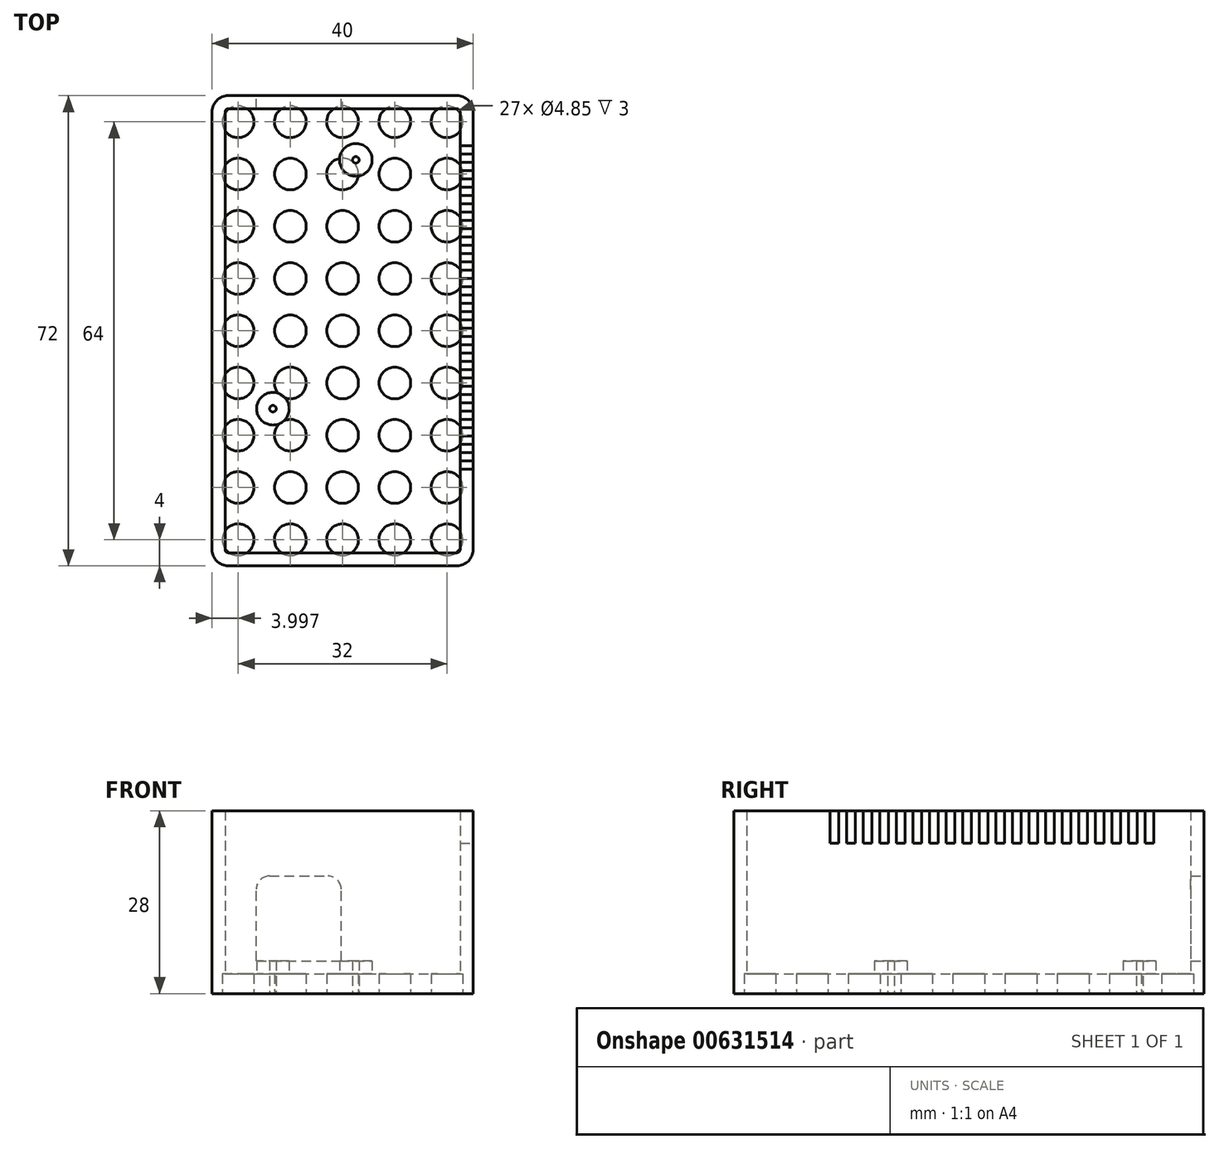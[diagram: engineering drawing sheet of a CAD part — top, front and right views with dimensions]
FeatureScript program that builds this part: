
annotation { "Feature Type Name" : "Feature", "Feature Type Description" : "" }
export const myFeature = defineFeature(function(context is Context, id is Id, definition is map)
    precondition{}
    {
        {
            var Q0;
            Q0=qCreatedBy(makeId("Top.planeOp"),FACE);
            var sketch = newSketch(context, id + "F0", { "sketchPlane" : qUnion([Q0])});
            skLineSegment(sketch, "E0", {"start": v(-12.71, -27.8) * mm, "end": v(-12.71, 30.62) * mm});
            skLineSegment(sketch, "E1", {"start": v(-12.71, 30.62) * mm, "end": v(15.23, 30.62) * mm});
            skLineSegment(sketch, "E2", {"start": v(15.23, -27.8) * mm, "end": v(15.23, 30.62) * mm});
            skLineSegment(sketch, "E3", {"start": v(-12.71, -27.8) * mm, "end": v(15.23, -27.8) * mm});
            skLineSegment(sketch, "E4", {"start": v(1, -18.66) * mm, "end": v(2.02, -18.66) * mm});
            skLineSegment(sketch, "E5", {"start": v(1.51, -19.16) * mm, "end": v(1.51, -18.15) * mm});
            skLineSegment(sketch, "E6", {"start": v(1, -16.12) * mm, "end": v(2.02, -16.12) * mm});
            skLineSegment(sketch, "E7", {"start": v(1.51, -16.62) * mm, "end": v(1.51, -15.6) * mm});
            skLineSegment(sketch, "E8", {"start": v(8.12, -3.92) * mm, "end": v(9.13, -3.92) * mm});
            skLineSegment(sketch, "E9", {"start": v(8.62, -4.43) * mm, "end": v(8.62, -3.42) * mm});
            skLineSegment(sketch, "E10", {"start": v(-11.7, -6.72) * mm, "end": v(-10.68, -6.72) * mm});
            skLineSegment(sketch, "E11", {"start": v(-11.19, -7.23) * mm, "end": v(-11.19, -6.21) * mm});
            skLineSegment(sketch, "E12", {"start": v(-9.16, -6.72) * mm, "end": v(-8.14, -6.72) * mm});
            skLineSegment(sketch, "E13", {"start": v(-8.65, -7.23) * mm, "end": v(-8.65, -6.21) * mm});
            skLineSegment(sketch, "E14", {"start": v(1.26, 12.46) * mm, "end": v(2.27, 12.46) * mm});
            skLineSegment(sketch, "E15", {"start": v(1.77, 11.95) * mm, "end": v(1.77, 12.97) * mm});
            skLineSegment(sketch, "E16", {"start": v(-1.28, 12.46) * mm, "end": v(-0.27, 12.46) * mm});
            skLineSegment(sketch, "E17", {"start": v(-0.77, 11.95) * mm, "end": v(-0.77, 12.97) * mm});
            skLineSegment(sketch, "E18", {"start": v(-4.87, 25.58) * mm, "end": v(-3.86, 25.58) * mm});
            skLineSegment(sketch, "E19", {"start": v(-4.37, 25.07) * mm, "end": v(-4.37, 26.09) * mm});
            skLineSegment(sketch, "E20", {"start": v(-9.27, 25.58) * mm, "end": v(-8.26, 25.58) * mm});
            skLineSegment(sketch, "E21", {"start": v(-8.77, 25.07) * mm, "end": v(-8.77, 26.09) * mm});
            skLineSegment(sketch, "E22", {"start": v(13.2, 16.4) * mm, "end": v(14.21, 16.4) * mm});
            skLineSegment(sketch, "E23", {"start": v(13.7, 15.89) * mm, "end": v(13.7, 16.9) * mm});
            skLineSegment(sketch, "E24", {"start": v(13.2, 18.94) * mm, "end": v(14.21, 18.94) * mm});
            skLineSegment(sketch, "E25", {"start": v(13.7, 18.43) * mm, "end": v(13.7, 19.44) * mm});
            skLineSegment(sketch, "E26", {"start": v(13.2, 21.48) * mm, "end": v(14.21, 21.48) * mm});
            skLineSegment(sketch, "E27", {"start": v(13.7, 20.97) * mm, "end": v(13.7, 21.98) * mm});
            skLineSegment(sketch, "E28", {"start": v(13.2, 24.02) * mm, "end": v(14.21, 24.02) * mm});
            skLineSegment(sketch, "E29", {"start": v(13.7, 23.5) * mm, "end": v(13.7, 24.52) * mm});
            skLineSegment(sketch, "E30", {"start": v(13.2, 26.56) * mm, "end": v(14.21, 26.56) * mm});
            skLineSegment(sketch, "E31", {"start": v(13.7, 26.05) * mm, "end": v(13.7, 27.06) * mm});
            skLineSegment(sketch, "E32", {"start": v(13.2, 29.1) * mm, "end": v(14.21, 29.1) * mm});
            skLineSegment(sketch, "E33", {"start": v(13.7, 28.59) * mm, "end": v(13.7, 29.6) * mm});
            skLineSegment(sketch, "E34", {"start": v(10.66, 16.4) * mm, "end": v(11.67, 16.4) * mm});
            skLineSegment(sketch, "E35", {"start": v(11.16, 15.89) * mm, "end": v(11.16, 16.9) * mm});
            skLineSegment(sketch, "E36", {"start": v(10.66, 18.94) * mm, "end": v(11.67, 18.94) * mm});
            skLineSegment(sketch, "E37", {"start": v(11.16, 18.43) * mm, "end": v(11.16, 19.44) * mm});
            skLineSegment(sketch, "E38", {"start": v(10.66, 21.48) * mm, "end": v(11.67, 21.48) * mm});
            skLineSegment(sketch, "E39", {"start": v(11.16, 20.97) * mm, "end": v(11.16, 21.98) * mm});
            skLineSegment(sketch, "E40", {"start": v(10.66, 24.02) * mm, "end": v(11.67, 24.02) * mm});
            skLineSegment(sketch, "E41", {"start": v(11.16, 23.5) * mm, "end": v(11.16, 24.52) * mm});
            skLineSegment(sketch, "E42", {"start": v(10.66, 26.56) * mm, "end": v(11.67, 26.56) * mm});
            skLineSegment(sketch, "E43", {"start": v(11.16, 26.05) * mm, "end": v(11.16, 27.06) * mm});
            skLineSegment(sketch, "E44", {"start": v(10.66, 29.1) * mm, "end": v(11.67, 29.1) * mm});
            skLineSegment(sketch, "E45", {"start": v(11.16, 28.59) * mm, "end": v(11.16, 29.6) * mm});
            skLineSegment(sketch, "E46", {"start": v(8.12, 29.1) * mm, "end": v(9.13, 29.1) * mm});
            skLineSegment(sketch, "E47", {"start": v(8.62, 28.59) * mm, "end": v(8.62, 29.6) * mm});
            skLineSegment(sketch, "E48", {"start": v(8.12, 26.56) * mm, "end": v(9.13, 26.56) * mm});
            skLineSegment(sketch, "E49", {"start": v(8.62, 26.05) * mm, "end": v(8.62, 27.06) * mm});
            skLineSegment(sketch, "E50", {"start": v(8.12, 24.02) * mm, "end": v(9.13, 24.02) * mm});
            skLineSegment(sketch, "E51", {"start": v(8.62, 23.5) * mm, "end": v(8.62, 24.52) * mm});
            skLineSegment(sketch, "E52", {"start": v(8.12, 21.48) * mm, "end": v(9.13, 21.48) * mm});
            skLineSegment(sketch, "E53", {"start": v(8.62, 20.97) * mm, "end": v(8.62, 21.98) * mm});
            skLineSegment(sketch, "E54", {"start": v(8.12, 18.94) * mm, "end": v(9.13, 18.94) * mm});
            skLineSegment(sketch, "E55", {"start": v(8.62, 18.43) * mm, "end": v(8.62, 19.44) * mm});
            skLineSegment(sketch, "E56", {"start": v(8.12, 16.4) * mm, "end": v(9.13, 16.4) * mm});
            skLineSegment(sketch, "E57", {"start": v(8.62, 15.89) * mm, "end": v(8.62, 16.9) * mm});
            skLineSegment(sketch, "E58", {"start": v(13.2, 13.86) * mm, "end": v(14.21, 13.86) * mm});
            skLineSegment(sketch, "E59", {"start": v(13.7, 13.35) * mm, "end": v(13.7, 14.36) * mm});
            skLineSegment(sketch, "E60", {"start": v(10.66, 13.86) * mm, "end": v(11.67, 13.86) * mm});
            skLineSegment(sketch, "E61", {"start": v(11.16, 13.35) * mm, "end": v(11.16, 14.36) * mm});
            skLineSegment(sketch, "E62", {"start": v(-11.7, 9.8) * mm, "end": v(-10.68, 9.8) * mm});
            skLineSegment(sketch, "E63", {"start": v(-11.19, 9.28) * mm, "end": v(-11.19, 10.3) * mm});
            skLineSegment(sketch, "E64", {"start": v(-11.7, 12.33) * mm, "end": v(-10.68, 12.33) * mm});
            skLineSegment(sketch, "E65", {"start": v(-11.19, 11.82) * mm, "end": v(-11.19, 12.84) * mm});
            skLineSegment(sketch, "E66", {"start": v(-11.7, 14.87) * mm, "end": v(-10.68, 14.87) * mm});
            skLineSegment(sketch, "E67", {"start": v(-11.19, 14.36) * mm, "end": v(-11.19, 15.38) * mm});
            skLineSegment(sketch, "E68", {"start": v(-11.7, 17.41) * mm, "end": v(-10.68, 17.41) * mm});
            skLineSegment(sketch, "E69", {"start": v(-11.19, 16.9) * mm, "end": v(-11.19, 17.92) * mm});
            skLineSegment(sketch, "E70", {"start": v(-11.7, 19.95) * mm, "end": v(-10.68, 19.95) * mm});
            skLineSegment(sketch, "E71", {"start": v(-11.19, 19.44) * mm, "end": v(-11.19, 20.46) * mm});
            skLineSegment(sketch, "E72", {"start": v(-11.7, 7.25) * mm, "end": v(-10.68, 7.25) * mm});
            skLineSegment(sketch, "E73", {"start": v(-11.19, 6.74) * mm, "end": v(-11.19, 7.76) * mm});
            skLineSegment(sketch, "E74", {"start": v(-11.7, 4.71) * mm, "end": v(-10.68, 4.71) * mm});
            skLineSegment(sketch, "E75", {"start": v(-11.19, 4.2) * mm, "end": v(-11.19, 5.22) * mm});
            skLineSegment(sketch, "E76", {"start": v(13.2, -1.38) * mm, "end": v(14.21, -1.38) * mm});
            skLineSegment(sketch, "E77", {"start": v(13.7, -1.9) * mm, "end": v(13.7, -0.88) * mm});
            skLineSegment(sketch, "E78", {"start": v(13.2, 1.16) * mm, "end": v(14.21, 1.16) * mm});
            skLineSegment(sketch, "E79", {"start": v(13.7, 0.65) * mm, "end": v(13.7, 1.66) * mm});
            skLineSegment(sketch, "E80", {"start": v(13.2, 3.7) * mm, "end": v(14.21, 3.7) * mm});
            skLineSegment(sketch, "E81", {"start": v(13.7, 3.19) * mm, "end": v(13.7, 4.2) * mm});
            skLineSegment(sketch, "E82", {"start": v(13.2, 6.24) * mm, "end": v(14.21, 6.24) * mm});
            skLineSegment(sketch, "E83", {"start": v(13.7, 5.73) * mm, "end": v(13.7, 6.74) * mm});
            skLineSegment(sketch, "E84", {"start": v(13.2, 8.78) * mm, "end": v(14.21, 8.78) * mm});
            skLineSegment(sketch, "E85", {"start": v(13.7, 8.27) * mm, "end": v(13.7, 9.28) * mm});
            skLineSegment(sketch, "E86", {"start": v(13.2, 11.32) * mm, "end": v(14.21, 11.32) * mm});
            skLineSegment(sketch, "E87", {"start": v(13.7, 10.8) * mm, "end": v(13.7, 11.82) * mm});
            skLineSegment(sketch, "E88", {"start": v(10.66, -1.38) * mm, "end": v(11.67, -1.38) * mm});
            skLineSegment(sketch, "E89", {"start": v(11.16, -1.9) * mm, "end": v(11.16, -0.88) * mm});
            skLineSegment(sketch, "E90", {"start": v(10.66, 1.16) * mm, "end": v(11.67, 1.16) * mm});
            skLineSegment(sketch, "E91", {"start": v(11.16, 0.65) * mm, "end": v(11.16, 1.66) * mm});
            skLineSegment(sketch, "E92", {"start": v(10.66, 3.7) * mm, "end": v(11.67, 3.7) * mm});
            skLineSegment(sketch, "E93", {"start": v(11.16, 3.19) * mm, "end": v(11.16, 4.2) * mm});
            skLineSegment(sketch, "E94", {"start": v(10.66, 6.24) * mm, "end": v(11.67, 6.24) * mm});
            skLineSegment(sketch, "E95", {"start": v(11.16, 5.73) * mm, "end": v(11.16, 6.74) * mm});
            skLineSegment(sketch, "E96", {"start": v(10.66, 8.78) * mm, "end": v(11.67, 8.78) * mm});
            skLineSegment(sketch, "E97", {"start": v(11.16, 8.27) * mm, "end": v(11.16, 9.28) * mm});
            skLineSegment(sketch, "E98", {"start": v(10.66, 11.32) * mm, "end": v(11.67, 11.32) * mm});
            skLineSegment(sketch, "E99", {"start": v(11.16, 10.8) * mm, "end": v(11.16, 11.82) * mm});
            skLineSegment(sketch, "E100", {"start": v(8.12, 11.32) * mm, "end": v(9.13, 11.32) * mm});
            skLineSegment(sketch, "E101", {"start": v(8.62, 10.8) * mm, "end": v(8.62, 11.82) * mm});
            skLineSegment(sketch, "E102", {"start": v(8.12, 8.78) * mm, "end": v(9.13, 8.78) * mm});
            skLineSegment(sketch, "E103", {"start": v(8.62, 8.27) * mm, "end": v(8.62, 9.28) * mm});
            skLineSegment(sketch, "E104", {"start": v(8.12, 6.24) * mm, "end": v(9.13, 6.24) * mm});
            skLineSegment(sketch, "E105", {"start": v(8.62, 5.73) * mm, "end": v(8.62, 6.74) * mm});
            skLineSegment(sketch, "E106", {"start": v(8.12, 3.7) * mm, "end": v(9.13, 3.7) * mm});
            skLineSegment(sketch, "E107", {"start": v(8.62, 3.19) * mm, "end": v(8.62, 4.2) * mm});
            skLineSegment(sketch, "E108", {"start": v(8.12, 1.16) * mm, "end": v(9.13, 1.16) * mm});
            skLineSegment(sketch, "E109", {"start": v(8.62, 0.65) * mm, "end": v(8.62, 1.66) * mm});
            skLineSegment(sketch, "E110", {"start": v(8.12, -1.38) * mm, "end": v(9.13, -1.38) * mm});
            skLineSegment(sketch, "E111", {"start": v(8.62, -1.9) * mm, "end": v(8.62, -0.88) * mm});
            skLineSegment(sketch, "E112", {"start": v(13.2, -3.92) * mm, "end": v(14.21, -3.92) * mm});
            skLineSegment(sketch, "E113", {"start": v(13.7, -4.43) * mm, "end": v(13.7, -3.42) * mm});
            skLineSegment(sketch, "E114", {"start": v(10.66, -3.92) * mm, "end": v(11.67, -3.92) * mm});
            skLineSegment(sketch, "E115", {"start": v(11.16, -4.43) * mm, "end": v(11.16, -3.42) * mm});
            skLineSegment(sketch, "E116", {"start": v(-11.26, -10.53) * mm, "end": v(-9.08, -10.53) * mm});
            skLineSegment(sketch, "E117", {"start": v(-10.17, -11.62) * mm, "end": v(-10.17, -9.44) * mm});
            skLineSegment(sketch, "E118", {"start": v(1.44, 27.57) * mm, "end": v(3.62, 27.57) * mm});
            skLineSegment(sketch, "E119", {"start": v(2.53, 26.48) * mm, "end": v(2.53, 28.66) * mm});
            skLineSegment(sketch, "E120", {"start": v(8.12, 13.86) * mm, "end": v(9.13, 13.86) * mm});
            skLineSegment(sketch, "E121", {"start": v(8.62, 13.35) * mm, "end": v(8.62, 14.36) * mm});
            skLineSegment(sketch, "E122", {"start": v(13.2, -19.16) * mm, "end": v(14.21, -19.16) * mm});
            skLineSegment(sketch, "E123", {"start": v(13.7, -19.67) * mm, "end": v(13.7, -18.66) * mm});
            skLineSegment(sketch, "E124", {"start": v(13.2, -16.62) * mm, "end": v(14.21, -16.62) * mm});
            skLineSegment(sketch, "E125", {"start": v(13.7, -17.13) * mm, "end": v(13.7, -16.12) * mm});
            skLineSegment(sketch, "E126", {"start": v(13.2, -14.08) * mm, "end": v(14.21, -14.08) * mm});
            skLineSegment(sketch, "E127", {"start": v(13.7, -14.6) * mm, "end": v(13.7, -13.58) * mm});
            skLineSegment(sketch, "E128", {"start": v(13.2, -11.54) * mm, "end": v(14.21, -11.54) * mm});
            skLineSegment(sketch, "E129", {"start": v(13.7, -12.05) * mm, "end": v(13.7, -11.04) * mm});
            skLineSegment(sketch, "E130", {"start": v(13.2, -9) * mm, "end": v(14.21, -9) * mm});
            skLineSegment(sketch, "E131", {"start": v(13.7, -9.51) * mm, "end": v(13.7, -8.5) * mm});
            skLineSegment(sketch, "E132", {"start": v(13.2, -6.46) * mm, "end": v(14.21, -6.46) * mm});
            skLineSegment(sketch, "E133", {"start": v(13.7, -6.97) * mm, "end": v(13.7, -5.96) * mm});
            skLineSegment(sketch, "E134", {"start": v(10.66, -19.16) * mm, "end": v(11.67, -19.16) * mm});
            skLineSegment(sketch, "E135", {"start": v(11.16, -19.67) * mm, "end": v(11.16, -18.66) * mm});
            skLineSegment(sketch, "E136", {"start": v(10.66, -16.62) * mm, "end": v(11.67, -16.62) * mm});
            skLineSegment(sketch, "E137", {"start": v(11.16, -17.13) * mm, "end": v(11.16, -16.12) * mm});
            skLineSegment(sketch, "E138", {"start": v(10.66, -14.08) * mm, "end": v(11.67, -14.08) * mm});
            skLineSegment(sketch, "E139", {"start": v(11.16, -14.6) * mm, "end": v(11.16, -13.58) * mm});
            skLineSegment(sketch, "E140", {"start": v(10.66, -11.54) * mm, "end": v(11.67, -11.54) * mm});
            skLineSegment(sketch, "E141", {"start": v(11.16, -12.05) * mm, "end": v(11.16, -11.04) * mm});
            skLineSegment(sketch, "E142", {"start": v(10.66, -9) * mm, "end": v(11.67, -9) * mm});
            skLineSegment(sketch, "E143", {"start": v(11.16, -9.51) * mm, "end": v(11.16, -8.5) * mm});
            skLineSegment(sketch, "E144", {"start": v(10.66, -6.46) * mm, "end": v(11.67, -6.46) * mm});
            skLineSegment(sketch, "E145", {"start": v(11.16, -6.97) * mm, "end": v(11.16, -5.96) * mm});
            skLineSegment(sketch, "E146", {"start": v(8.12, -6.46) * mm, "end": v(9.13, -6.46) * mm});
            skLineSegment(sketch, "E147", {"start": v(8.62, -6.97) * mm, "end": v(8.62, -5.96) * mm});
            skLineSegment(sketch, "E148", {"start": v(8.12, -9) * mm, "end": v(9.13, -9) * mm});
            skLineSegment(sketch, "E149", {"start": v(8.62, -9.51) * mm, "end": v(8.62, -8.5) * mm});
            skLineSegment(sketch, "E150", {"start": v(8.12, -11.54) * mm, "end": v(9.13, -11.54) * mm});
            skLineSegment(sketch, "E151", {"start": v(8.62, -12.05) * mm, "end": v(8.62, -11.04) * mm});
            skLineSegment(sketch, "E152", {"start": v(8.12, -14.08) * mm, "end": v(9.13, -14.08) * mm});
            skLineSegment(sketch, "E153", {"start": v(8.62, -14.6) * mm, "end": v(8.62, -13.58) * mm});
            skLineSegment(sketch, "E154", {"start": v(8.12, -16.62) * mm, "end": v(9.13, -16.62) * mm});
            skLineSegment(sketch, "E155", {"start": v(8.62, -17.13) * mm, "end": v(8.62, -16.12) * mm});
            skLineSegment(sketch, "E156", {"start": v(8.12, -19.16) * mm, "end": v(9.13, -19.16) * mm});
            skLineSegment(sketch, "E157", {"start": v(8.62, -19.67) * mm, "end": v(8.62, -18.66) * mm});
            skLineSegment(sketch, "E158", {"start": v(4.81, -23.74) * mm, "end": v(5.83, -23.74) * mm});
            skLineSegment(sketch, "E159", {"start": v(5.32, -24.24) * mm, "end": v(5.32, -23.23) * mm});
            skLineSegment(sketch, "E160", {"start": v(4.81, -26.28) * mm, "end": v(5.83, -26.28) * mm});
            skLineSegment(sketch, "E161", {"start": v(5.32, -26.78) * mm, "end": v(5.32, -25.77) * mm});
            skLineSegment(sketch, "E162", {"start": v(-11.7, -26.28) * mm, "end": v(-10.68, -26.28) * mm});
            skLineSegment(sketch, "E163", {"start": v(-11.19, -26.78) * mm, "end": v(-11.19, -25.77) * mm});
            skLineSegment(sketch, "E164", {"start": v(-9.16, -26.28) * mm, "end": v(-8.14, -26.28) * mm});
            skLineSegment(sketch, "E165", {"start": v(-8.65, -26.78) * mm, "end": v(-8.65, -25.77) * mm});
            skLineSegment(sketch, "E166", {"start": v(-6.62, -26.28) * mm, "end": v(-5.6, -26.28) * mm});
            skLineSegment(sketch, "E167", {"start": v(-6.1, -26.78) * mm, "end": v(-6.1, -25.77) * mm});
            skLineSegment(sketch, "E168", {"start": v(-4.08, -26.28) * mm, "end": v(-3.06, -26.28) * mm});
            skLineSegment(sketch, "E169", {"start": v(-3.57, -26.78) * mm, "end": v(-3.57, -25.77) * mm});
            skLineSegment(sketch, "E170", {"start": v(-1.54, -26.28) * mm, "end": v(-0.52, -26.28) * mm});
            skLineSegment(sketch, "E171", {"start": v(-1.03, -26.78) * mm, "end": v(-1.03, -25.77) * mm});
            skLineSegment(sketch, "E172", {"start": v(1, -26.28) * mm, "end": v(2.02, -26.28) * mm});
            skLineSegment(sketch, "E173", {"start": v(1.51, -26.78) * mm, "end": v(1.51, -25.77) * mm});
            skLineSegment(sketch, "E174", {"start": v(-11.7, -23.74) * mm, "end": v(-10.68, -23.74) * mm});
            skLineSegment(sketch, "E175", {"start": v(-11.19, -24.24) * mm, "end": v(-11.19, -23.23) * mm});
            skLineSegment(sketch, "E176", {"start": v(-9.16, -23.74) * mm, "end": v(-8.14, -23.74) * mm});
            skLineSegment(sketch, "E177", {"start": v(-8.65, -24.24) * mm, "end": v(-8.65, -23.23) * mm});
            skLineSegment(sketch, "E178", {"start": v(-6.62, -23.74) * mm, "end": v(-5.6, -23.74) * mm});
            skLineSegment(sketch, "E179", {"start": v(-6.1, -24.24) * mm, "end": v(-6.1, -23.23) * mm});
            skLineSegment(sketch, "E180", {"start": v(-4.08, -23.74) * mm, "end": v(-3.06, -23.74) * mm});
            skLineSegment(sketch, "E181", {"start": v(-3.57, -24.24) * mm, "end": v(-3.57, -23.23) * mm});
            skLineSegment(sketch, "E182", {"start": v(-1.54, -23.74) * mm, "end": v(-0.52, -23.74) * mm});
            skLineSegment(sketch, "E183", {"start": v(-1.03, -24.24) * mm, "end": v(-1.03, -23.23) * mm});
            skLineSegment(sketch, "E184", {"start": v(1, -23.74) * mm, "end": v(2.02, -23.74) * mm});
            skLineSegment(sketch, "E185", {"start": v(1.51, -24.24) * mm, "end": v(1.51, -23.23) * mm});
            skLineSegment(sketch, "E186", {"start": v(1, -21.2) * mm, "end": v(2.02, -21.2) * mm});
            skLineSegment(sketch, "E187", {"start": v(1.51, -21.7) * mm, "end": v(1.51, -20.69) * mm});
            skLineSegment(sketch, "E188", {"start": v(-1.54, -21.2) * mm, "end": v(-0.52, -21.2) * mm});
            skLineSegment(sketch, "E189", {"start": v(-1.03, -21.7) * mm, "end": v(-1.03, -20.69) * mm});
            skLineSegment(sketch, "E190", {"start": v(-4.08, -21.2) * mm, "end": v(-3.06, -21.2) * mm});
            skLineSegment(sketch, "E191", {"start": v(-3.57, -21.7) * mm, "end": v(-3.57, -20.69) * mm});
            skLineSegment(sketch, "E192", {"start": v(-6.62, -21.2) * mm, "end": v(-5.6, -21.2) * mm});
            skLineSegment(sketch, "E193", {"start": v(-6.1, -21.7) * mm, "end": v(-6.1, -20.69) * mm});
            skLineSegment(sketch, "E194", {"start": v(-9.16, -21.2) * mm, "end": v(-8.14, -21.2) * mm});
            skLineSegment(sketch, "E195", {"start": v(-8.65, -21.7) * mm, "end": v(-8.65, -20.69) * mm});
            skLineSegment(sketch, "E196", {"start": v(-11.7, -21.2) * mm, "end": v(-10.68, -21.2) * mm});
            skLineSegment(sketch, "E197", {"start": v(-11.19, -21.7) * mm, "end": v(-11.19, -20.69) * mm});
            skLineSegment(sketch, "E198", {"start": v(8.93, -24.12) * mm, "end": v(10.46, -24.12) * mm});
            skLineSegment(sketch, "E199", {"start": v(9.7, -24.88) * mm, "end": v(9.7, -23.36) * mm});
            skLineSegment(sketch, "E200", {"start": v(12.43, -24.12) * mm, "end": v(13.96, -24.12) * mm});
            skLineSegment(sketch, "E201", {"start": v(13.2, -24.88) * mm, "end": v(13.2, -23.36) * mm});
            skLineSegment(sketch, "E202", {"start": v(3.54, -18.66) * mm, "end": v(4.56, -18.66) * mm});
            skLineSegment(sketch, "E203", {"start": v(4.05, -19.16) * mm, "end": v(4.05, -18.15) * mm});
            skLineSegment(sketch, "E204", {"start": v(3.54, -21.2) * mm, "end": v(4.56, -21.2) * mm});
            skLineSegment(sketch, "E205", {"start": v(4.05, -21.7) * mm, "end": v(4.05, -20.69) * mm});
            skLineSegment(sketch, "E206", {"start": v(-11.7, -18.66) * mm, "end": v(-10.68, -18.66) * mm});
            skLineSegment(sketch, "E207", {"start": v(-11.19, -19.16) * mm, "end": v(-11.19, -18.15) * mm});
            skLineSegment(sketch, "E208", {"start": v(-11.7, -16.12) * mm, "end": v(-10.68, -16.12) * mm});
            skLineSegment(sketch, "E209", {"start": v(-11.19, -16.62) * mm, "end": v(-11.19, -15.6) * mm});
            skLineSegment(sketch, "E210", {"start": v(-9.16, -18.66) * mm, "end": v(-8.14, -18.66) * mm});
            skLineSegment(sketch, "E211", {"start": v(-8.65, -19.16) * mm, "end": v(-8.65, -18.15) * mm});
            skLineSegment(sketch, "E212", {"start": v(-9.16, -16.12) * mm, "end": v(-8.14, -16.12) * mm});
            skLineSegment(sketch, "E213", {"start": v(-8.65, -16.62) * mm, "end": v(-8.65, -15.6) * mm});
            skLineSegment(sketch, "E214", {"start": v(-6.62, -18.66) * mm, "end": v(-5.6, -18.66) * mm});
            skLineSegment(sketch, "E215", {"start": v(-6.1, -19.16) * mm, "end": v(-6.1, -18.15) * mm});
            skLineSegment(sketch, "E216", {"start": v(-6.62, -16.12) * mm, "end": v(-5.6, -16.12) * mm});
            skLineSegment(sketch, "E217", {"start": v(-6.1, -16.62) * mm, "end": v(-6.1, -15.6) * mm});
            skLineSegment(sketch, "E218", {"start": v(-4.08, -18.66) * mm, "end": v(-3.06, -18.66) * mm});
            skLineSegment(sketch, "E219", {"start": v(-3.57, -19.16) * mm, "end": v(-3.57, -18.15) * mm});
            skLineSegment(sketch, "E220", {"start": v(-4.08, -16.12) * mm, "end": v(-3.06, -16.12) * mm});
            skLineSegment(sketch, "E221", {"start": v(-3.57, -16.62) * mm, "end": v(-3.57, -15.6) * mm});
            skLineSegment(sketch, "E222", {"start": v(-1.54, -18.66) * mm, "end": v(-0.52, -18.66) * mm});
            skLineSegment(sketch, "E223", {"start": v(-1.03, -19.16) * mm, "end": v(-1.03, -18.15) * mm});
            skLineSegment(sketch, "E224", {"start": v(-1.54, -16.12) * mm, "end": v(-0.52, -16.12) * mm});
            skLineSegment(sketch, "E225", {"start": v(-1.03, -16.62) * mm, "end": v(-1.03, -15.6) * mm});
            skLineSegment(sketch, "E226", {"start": v(6.15, -16.37) * mm, "end": v(6.53, -16.37) * mm});
            skLineSegment(sketch, "E227", {"start": v(6.34, -16.56) * mm, "end": v(6.34, -16.18) * mm});
            skLineSegment(sketch, "E228", {"start": v(5.26, -0.24) * mm, "end": v(5.64, -0.24) * mm});
            skLineSegment(sketch, "E229", {"start": v(5.45, -0.43) * mm, "end": v(5.45, -0.05) * mm});
            skLineSegment(sketch, "E230", {"start": v(-7.19, 0.27) * mm, "end": v(-6.8, 0.27) * mm});
            skLineSegment(sketch, "E231", {"start": v(-7, 0.08) * mm, "end": v(-7, 0.46) * mm});
            skLineSegment(sketch, "E232", {"start": v(-6.55, 1.03) * mm, "end": v(-6.17, 1.03) * mm});
            skLineSegment(sketch, "E233", {"start": v(-6.36, 0.84) * mm, "end": v(-6.36, 1.22) * mm});
            skLineSegment(sketch, "E234", {"start": v(-6.3, 2.04) * mm, "end": v(-5.92, 2.04) * mm});
            skLineSegment(sketch, "E235", {"start": v(-6.1, 1.85) * mm, "end": v(-6.1, 2.24) * mm});
            skLineSegment(sketch, "E236", {"start": v(-6.3, 5.35) * mm, "end": v(-5.92, 5.35) * mm});
            skLineSegment(sketch, "E237", {"start": v(-6.1, 5.16) * mm, "end": v(-6.1, 5.54) * mm});
            skLineSegment(sketch, "E238", {"start": v(-6.3, 4.2) * mm, "end": v(-5.92, 4.2) * mm});
            skLineSegment(sketch, "E239", {"start": v(-6.1, 4.01) * mm, "end": v(-6.1, 4.4) * mm});
            skLineSegment(sketch, "E240", {"start": v(-10.87, 2.17) * mm, "end": v(-10.5, 2.17) * mm});
            skLineSegment(sketch, "E241", {"start": v(-10.68, 1.98) * mm, "end": v(-10.68, 2.36) * mm});
            skLineSegment(sketch, "E242", {"start": v(-3.63, -6.08) * mm, "end": v(-3.25, -6.08) * mm});
            skLineSegment(sketch, "E243", {"start": v(-3.44, -6.27) * mm, "end": v(-3.44, -5.9) * mm});
            skLineSegment(sketch, "E244", {"start": v(-4.14, 11.57) * mm, "end": v(-3.76, 11.57) * mm});
            skLineSegment(sketch, "E245", {"start": v(-3.95, 11.38) * mm, "end": v(-3.95, 11.76) * mm});
            skLineSegment(sketch, "E246", {"start": v(5.38, 24.27) * mm, "end": v(5.77, 24.27) * mm});
            skLineSegment(sketch, "E247", {"start": v(5.58, 24.08) * mm, "end": v(5.58, 24.46) * mm});
            skLineSegment(sketch, "E248", {"start": v(5.38, 21.1) * mm, "end": v(5.77, 21.1) * mm});
            skLineSegment(sketch, "E249", {"start": v(5.58, 20.9) * mm, "end": v(5.58, 21.29) * mm});
            skLineSegment(sketch, "E250", {"start": v(6.9, 27.32) * mm, "end": v(7.29, 27.32) * mm});
            skLineSegment(sketch, "E251", {"start": v(7.1, 27.13) * mm, "end": v(7.1, 27.5) * mm});
            skLineSegment(sketch, "E252", {"start": v(6.9, 9.8) * mm, "end": v(7.29, 9.8) * mm});
            skLineSegment(sketch, "E253", {"start": v(7.1, 9.6) * mm, "end": v(7.1, 9.98) * mm});
            skLineSegment(sketch, "E254", {"start": v(3.99, 5.98) * mm, "end": v(4.37, 5.98) * mm});
            skLineSegment(sketch, "E255", {"start": v(4.18, 5.8) * mm, "end": v(4.18, 6.17) * mm});
            skLineSegment(sketch, "E256", {"start": v(5, 6.24) * mm, "end": v(5.38, 6.24) * mm});
            skLineSegment(sketch, "E257", {"start": v(5.2, 6.05) * mm, "end": v(5.2, 6.43) * mm});
            skLineSegment(sketch, "E258", {"start": v(5.1, 4.64) * mm, "end": v(5.49, 4.64) * mm});
            skLineSegment(sketch, "E259", {"start": v(5.3, 4.45) * mm, "end": v(5.3, 4.83) * mm});
            skLineSegment(sketch, "E260", {"start": v(3.23, 6.74) * mm, "end": v(3.6, 6.74) * mm});
            skLineSegment(sketch, "E261", {"start": v(3.42, 6.55) * mm, "end": v(3.42, 6.93) * mm});
            skLineSegment(sketch, "E262", {"start": v(5.1, 3.64) * mm, "end": v(5.49, 3.64) * mm});
            skLineSegment(sketch, "E263", {"start": v(5.3, 3.45) * mm, "end": v(5.3, 3.84) * mm});
            skLineSegment(sketch, "E264", {"start": v(6.73, 6.92) * mm, "end": v(7.11, 6.92) * mm});
            skLineSegment(sketch, "E265", {"start": v(6.92, 6.73) * mm, "end": v(6.92, 7.11) * mm});
            skLineSegment(sketch, "E266", {"start": v(6.9, 4.84) * mm, "end": v(7.29, 4.84) * mm});
            skLineSegment(sketch, "E267", {"start": v(7.1, 4.65) * mm, "end": v(7.1, 5.03) * mm});
            skLineSegment(sketch, "E268", {"start": v(4.11, -3.04) * mm, "end": v(4.5, -3.04) * mm});
            skLineSegment(sketch, "E269", {"start": v(4.3, -3.23) * mm, "end": v(4.3, -2.84) * mm});
            skLineSegment(sketch, "E270", {"start": v(4.78, 2.7) * mm, "end": v(5.16, 2.7) * mm});
            skLineSegment(sketch, "E271", {"start": v(4.97, 2.51) * mm, "end": v(4.97, 2.9) * mm});
            skLineSegment(sketch, "E272", {"start": v(4.62, -2.15) * mm, "end": v(5, -2.15) * mm});
            skLineSegment(sketch, "E273", {"start": v(4.81, -2.34) * mm, "end": v(4.81, -1.96) * mm});
            skLineSegment(sketch, "E274", {"start": v(9.32, 27.83) * mm, "end": v(9.7, 27.83) * mm});
            skLineSegment(sketch, "E275", {"start": v(9.51, 27.64) * mm, "end": v(9.51, 28.02) * mm});
            skLineSegment(sketch, "E276", {"start": v(5.1, 1.77) * mm, "end": v(5.49, 1.77) * mm});
            skLineSegment(sketch, "E277", {"start": v(5.3, 1.57) * mm, "end": v(5.3, 1.96) * mm});
            skLineSegment(sketch, "E278", {"start": v(5.05, 0.77) * mm, "end": v(5.44, 0.77) * mm});
            skLineSegment(sketch, "E279", {"start": v(5.25, 0.58) * mm, "end": v(5.25, 0.97) * mm});
            skLineSegment(sketch, "E280", {"start": v(4.62, 20.33) * mm, "end": v(5, 20.33) * mm});
            skLineSegment(sketch, "E281", {"start": v(4.81, 20.14) * mm, "end": v(4.81, 20.52) * mm});
            skLineSegment(sketch, "E282", {"start": v(5.26, 22.5) * mm, "end": v(5.64, 22.5) * mm});
            skLineSegment(sketch, "E283", {"start": v(5.45, 22.3) * mm, "end": v(5.45, 22.68) * mm});
            skLineSegment(sketch, "E284", {"start": v(5, 25.54) * mm, "end": v(5.38, 25.54) * mm});
            skLineSegment(sketch, "E285", {"start": v(5.2, 25.35) * mm, "end": v(5.2, 25.73) * mm});
            skLineSegment(sketch, "E286", {"start": v(4.11, 13.35) * mm, "end": v(4.5, 13.35) * mm});
            skLineSegment(sketch, "E287", {"start": v(4.3, 13.16) * mm, "end": v(4.3, 13.54) * mm});
            skLineSegment(sketch, "E288", {"start": v(0.46, -4.18) * mm, "end": v(0.84, -4.18) * mm});
            skLineSegment(sketch, "E289", {"start": v(0.65, -4.37) * mm, "end": v(0.65, -3.99) * mm});
            skLineSegment(sketch, "E290", {"start": v(-0.52, -4.94) * mm, "end": v(-0.14, -4.94) * mm});
            skLineSegment(sketch, "E291", {"start": v(-0.33, -5.13) * mm, "end": v(-0.33, -4.75) * mm});
            skLineSegment(sketch, "E292", {"start": v(-6.8, -1.9) * mm, "end": v(-6.43, -1.9) * mm});
            skLineSegment(sketch, "E293", {"start": v(-6.62, -2.08) * mm, "end": v(-6.62, -1.7) * mm});
            skLineSegment(sketch, "E294", {"start": v(-7.19, -0.88) * mm, "end": v(-6.8, -0.88) * mm});
            skLineSegment(sketch, "E295", {"start": v(-7, -1.07) * mm, "end": v(-7, -0.69) * mm});
            skLineSegment(sketch, "E296", {"start": v(-7.82, -3.54) * mm, "end": v(-7.44, -3.54) * mm});
            skLineSegment(sketch, "E297", {"start": v(-7.63, -3.73) * mm, "end": v(-7.63, -3.35) * mm});
            skLineSegment(sketch, "E298", {"start": v(-0.46, 7.89) * mm, "end": v(-0.08, 7.89) * mm});
            skLineSegment(sketch, "E299", {"start": v(-0.27, 7.7) * mm, "end": v(-0.27, 8.08) * mm});
            skLineSegment(sketch, "E300", {"start": v(-5.8, 6.74) * mm, "end": v(-5.41, 6.74) * mm});
            skLineSegment(sketch, "E301", {"start": v(-5.6, 6.55) * mm, "end": v(-5.6, 6.93) * mm});
            skLineSegment(sketch, "E302", {"start": v(-5.92, 27.32) * mm, "end": v(-5.54, 27.32) * mm});
            skLineSegment(sketch, "E303", {"start": v(-5.73, 27.13) * mm, "end": v(-5.73, 27.5) * mm});
            skLineSegment(sketch, "E304", {"start": v(-7.57, 27.32) * mm, "end": v(-7.19, 27.32) * mm});
            skLineSegment(sketch, "E305", {"start": v(-7.38, 27.13) * mm, "end": v(-7.38, 27.5) * mm});
            skLineSegment(sketch, "E306", {"start": v(-10.1, 11.06) * mm, "end": v(-9.73, 11.06) * mm});
            skLineSegment(sketch, "E307", {"start": v(-9.92, 10.87) * mm, "end": v(-9.92, 11.25) * mm});
            skLineSegment(sketch, "E308", {"start": v(-8.46, 2.17) * mm, "end": v(-8.08, 2.17) * mm});
            skLineSegment(sketch, "E309", {"start": v(-8.27, 1.98) * mm, "end": v(-8.27, 2.36) * mm});
            skLineSegment(sketch, "E310", {"start": v(-7.82, 12.33) * mm, "end": v(-7.44, 12.33) * mm});
            skLineSegment(sketch, "E311", {"start": v(-7.63, 12.14) * mm, "end": v(-7.63, 12.52) * mm});
            skLineSegment(sketch, "E312", {"start": v(-0.46, 15) * mm, "end": v(-0.08, 15) * mm});
            skLineSegment(sketch, "E313", {"start": v(-0.27, 14.8) * mm, "end": v(-0.27, 15.19) * mm});
            skLineSegment(sketch, "E314", {"start": v(-2.74, 13.98) * mm, "end": v(-2.36, 13.98) * mm});
            skLineSegment(sketch, "E315", {"start": v(-2.55, 13.8) * mm, "end": v(-2.55, 14.17) * mm});
            skLineSegment(sketch, "E316", {"start": v(0.75, 16.9) * mm, "end": v(1.13, 16.9) * mm});
            skLineSegment(sketch, "E317", {"start": v(0.94, 16.71) * mm, "end": v(0.94, 17.1) * mm});
            skLineSegment(sketch, "E318", {"start": v(2.46, 18.3) * mm, "end": v(2.84, 18.3) * mm});
            skLineSegment(sketch, "E319", {"start": v(2.65, 18.11) * mm, "end": v(2.65, 18.5) * mm});
            skLineSegment(sketch, "E320", {"start": v(4.11, 18.3) * mm, "end": v(4.5, 18.3) * mm});
            skLineSegment(sketch, "E321", {"start": v(4.3, 18.11) * mm, "end": v(4.3, 18.5) * mm});
            skLineSegment(sketch, "E322", {"start": v(-1.73, 15.5) * mm, "end": v(-1.35, 15.5) * mm});
            skLineSegment(sketch, "E323", {"start": v(-1.54, 15.32) * mm, "end": v(-1.54, 15.7) * mm});
            skLineSegment(sketch, "E324", {"start": v(-5.16, 16.78) * mm, "end": v(-4.78, 16.78) * mm});
            skLineSegment(sketch, "E325", {"start": v(-4.97, 16.59) * mm, "end": v(-4.97, 16.97) * mm});
            skLineSegment(sketch, "E326", {"start": v(-8.33, 16.14) * mm, "end": v(-7.95, 16.14) * mm});
            skLineSegment(sketch, "E327", {"start": v(-8.14, 15.95) * mm, "end": v(-8.14, 16.33) * mm});
            skLineSegment(sketch, "E328", {"start": v(-2.36, 10.93) * mm, "end": v(-1.98, 10.93) * mm});
            skLineSegment(sketch, "E329", {"start": v(-2.17, 10.74) * mm, "end": v(-2.17, 11.13) * mm});
            skLineSegment(sketch, "E330", {"start": v(-0.58, -7.48) * mm, "end": v(-0.2, -7.48) * mm});
            skLineSegment(sketch, "E331", {"start": v(-0.4, -7.67) * mm, "end": v(-0.4, -7.29) * mm});
            skLineSegment(sketch, "E332", {"start": v(0.05, -8.24) * mm, "end": v(0.43, -8.24) * mm});
            skLineSegment(sketch, "E333", {"start": v(0.24, -8.43) * mm, "end": v(0.24, -8.05) * mm});
            skLineSegment(sketch, "E334", {"start": v(-3.12, -8.75) * mm, "end": v(-2.74, -8.75) * mm});
            skLineSegment(sketch, "E335", {"start": v(-2.93, -8.94) * mm, "end": v(-2.93, -8.56) * mm});
            skLineSegment(sketch, "E336", {"start": v(1.96, -13.96) * mm, "end": v(2.34, -13.96) * mm});
            skLineSegment(sketch, "E337", {"start": v(2.15, -14.15) * mm, "end": v(2.15, -13.77) * mm});
            skLineSegment(sketch, "E338", {"start": v(1.32, -12.3) * mm, "end": v(1.7, -12.3) * mm});
            skLineSegment(sketch, "E339", {"start": v(1.51, -12.5) * mm, "end": v(1.51, -12.12) * mm});
            skLineSegment(sketch, "E340", {"start": v(-2.62, -11.16) * mm, "end": v(-2.24, -11.16) * mm});
            skLineSegment(sketch, "E341", {"start": v(-2.43, -11.35) * mm, "end": v(-2.43, -10.97) * mm});
            skLineSegment(sketch, "E342", {"start": v(-6.43, -11.54) * mm, "end": v(-6.05, -11.54) * mm});
            skLineSegment(sketch, "E343", {"start": v(-6.24, -11.73) * mm, "end": v(-6.24, -11.35) * mm});
            skLineSegment(sketch, "E344", {"start": v(-5.41, -9) * mm, "end": v(-5.03, -9) * mm});
            skLineSegment(sketch, "E345", {"start": v(-5.22, -9.2) * mm, "end": v(-5.22, -8.81) * mm});
            skSolve(sketch);
        }
        {
            var Q0;
            Q0=qCreatedBy(makeId("Top.planeOp"),FACE);
            var sketch = newSketch(context, id + "F1", { "sketchPlane" : qUnion([Q0])});
            skPoint(sketch, "E346.0", {"position": v(-10.17, -10.53) * mm});
            skPoint(sketch, "E346.1", {"position": v(2.53, 27.57) * mm});
            skCircle(sketch, "E347", {"center": v(2.53, 27.57) * mm, "radius": 0.5 * mm});
            skCircle(sketch, "E348", {"center": v(-10.17, -10.53) * mm, "radius": 0.5 * mm});
            skLineSegment(sketch, "E349.0", {"start": v(-17, 37.4) * mm, "end": v(18, 37.4) * mm});
            skLineSegment(sketch, "E349.1", {"start": v(-19.5, -32.1) * mm, "end": v(-19.5, 34.9) * mm});
            skLineSegment(sketch, "E349.2", {"start": v(-17, -34.6) * mm, "end": v(18, -34.6) * mm});
            skLineSegment(sketch, "E349.3", {"start": v(20.5, -32.1) * mm, "end": v(20.5, 34.9) * mm});
            skPoint(sketch, "E350.visualSharp", {"position": v(-19.5, 37.4) * mm});
            skArc(sketch, "E350.filletArc", {"start": v(-17, 37.4) * mm, "mid": v(-18.77, 36.68) * mm, "end": v(-19.5, 34.9) * mm});
            skPoint(sketch, "E351.visualSharp", {"position": v(20.5, 37.4) * mm});
            skArc(sketch, "E351.filletArc", {"start": v(20.5, 34.9) * mm, "mid": v(19.77, 36.68) * mm, "end": v(18, 37.4) * mm});
            skPoint(sketch, "E352.visualSharp", {"position": v(20.5, -34.6) * mm});
            skArc(sketch, "E352.filletArc", {"start": v(18, -34.6) * mm, "mid": v(19.77, -33.86) * mm, "end": v(20.5, -32.1) * mm});
            skPoint(sketch, "E353.visualSharp", {"position": v(-19.5, -34.6) * mm});
            skArc(sketch, "E353.filletArc", {"start": v(-19.5, -32.1) * mm, "mid": v(-18.77, -33.86) * mm, "end": v(-17, -34.6) * mm});
            skSolve(sketch);
        }
        {
            var Q0;
            Q0 = qSketchRegion(id + "F1", true);
            extrude(context, id + "F2", {"entities" : qUnion([Q0]), "depth" : 3 * mm, "offsetDistance" : 25 * mm});
        }
        {
            var Q0;
            Q0=makeQuery(id+"F2.opExtrude","CAP_FACE",FACE,{"disambiguationData":[OSD([sQuery(id+"F1.wireOp",EDGE,"E347"),sQuery(id+"F1.wireOp",EDGE,"E348"),sQuery(id+"F1.wireOp",EDGE,"E349.0"),sQuery(id+"F1.wireOp",EDGE,"E349.1"),sQuery(id+"F1.wireOp",EDGE,"E349.2"),sQuery(id+"F1.wireOp",EDGE,"E349.3"),sQuery(id+"F1.wireOp",EDGE,"E350.filletArc"),sQuery(id+"F1.wireOp",EDGE,"E351.filletArc"),sQuery(id+"F1.wireOp",EDGE,"E352.filletArc"),sQuery(id+"F1.wireOp",EDGE,"E353.filletArc")])],"isStart":true});
            var sketch = newSketch(context, id + "F3", { "sketchPlane" : qUnion([Q0])});
            skLineSegment(sketch, "E354.bottom", {"start": v(-11.5, 26.6) * mm, "end": v(-19.5, 26.6) * mm, "construction": true});
            skLineSegment(sketch, "E354.top", {"start": v(-11.5, 34.6) * mm, "end": v(-19.5, 34.6) * mm, "construction": true});
            skLineSegment(sketch, "E354.left", {"start": v(-11.5, 26.6) * mm, "end": v(-11.5, 34.6) * mm, "construction": true});
            skLineSegment(sketch, "E354.right", {"start": v(-19.5, 26.6) * mm, "end": v(-19.5, 34.6) * mm, "construction": true});
            skLineSegment(sketch, "E355", {"start": v(-19.5, 34.6) * mm, "end": v(-11.5, 26.6) * mm, "construction": true});
            skCircle(sketch, "E356", {"center": v(-15.5, 30.6) * mm, "radius": 2.43 * mm});
            skCircle(sketch, "E357.0.1.0", {"center": v(-15.5, 22.6) * mm, "radius": 2.43 * mm});
            skCircle(sketch, "E357.1.0.0", {"center": v(-7.5, 30.6) * mm, "radius": 2.43 * mm});
            skCircle(sketch, "E357.1.1.0", {"center": v(-7.5, 22.6) * mm, "radius": 2.43 * mm});
            skCircle(sketch, "E357.2.0.0", {"center": v(0.5, 30.6) * mm, "radius": 2.43 * mm});
            skCircle(sketch, "E357.2.1.0", {"center": v(0.5, 22.6) * mm, "radius": 2.43 * mm});
            skLineSegment(sketch, "E357.direction1", {"start": v(-15.5, 30.6) * mm, "end": v(-7.5, 30.6) * mm, "construction": true});
            skLineSegment(sketch, "E357.direction2", {"start": v(-15.5, 30.6) * mm, "end": v(-15.5, 22.6) * mm, "construction": true});
            skCircle(sketch, "E358.0.3.0", {"center": v(8.5, 30.6) * mm, "radius": 2.43 * mm});
            skCircle(sketch, "E358.0.3.1", {"center": v(8.5, 22.6) * mm, "radius": 2.43 * mm});
            skCircle(sketch, "E358.0.4.0", {"center": v(16.5, 30.6) * mm, "radius": 2.43 * mm});
            skCircle(sketch, "E358.0.4.1", {"center": v(16.5, 22.6) * mm, "radius": 2.43 * mm});
            skCircle(sketch, "E359.0.0.2", {"center": v(-15.5, 14.6) * mm, "radius": 2.43 * mm});
            skCircle(sketch, "E359.0.0.3", {"center": v(-15.5, 6.6) * mm, "radius": 2.43 * mm});
            skCircle(sketch, "E359.0.0.4", {"center": v(-15.5, -1.4) * mm, "radius": 2.43 * mm});
            skCircle(sketch, "E359.0.0.5", {"center": v(-15.5, -9.4) * mm, "radius": 2.43 * mm});
            skCircle(sketch, "E359.0.0.6", {"center": v(-15.5, -17.4) * mm, "radius": 2.43 * mm});
            skCircle(sketch, "E359.0.0.7", {"center": v(-15.5, -25.4) * mm, "radius": 2.43 * mm});
            skCircle(sketch, "E359.0.0.8", {"center": v(-15.5, -33.4) * mm, "radius": 2.43 * mm});
            skCircle(sketch, "E359.0.1.2", {"center": v(-7.5, 14.6) * mm, "radius": 2.43 * mm});
            skCircle(sketch, "E359.0.1.3", {"center": v(-7.5, 6.6) * mm, "radius": 2.43 * mm});
            skCircle(sketch, "E359.0.1.4", {"center": v(-7.5, -1.4) * mm, "radius": 2.43 * mm});
            skCircle(sketch, "E359.0.1.5", {"center": v(-7.5, -9.4) * mm, "radius": 2.43 * mm});
            skCircle(sketch, "E359.0.1.6", {"center": v(-7.5, -17.4) * mm, "radius": 2.43 * mm});
            skCircle(sketch, "E359.0.1.7", {"center": v(-7.5, -25.4) * mm, "radius": 2.43 * mm});
            skCircle(sketch, "E359.0.1.8", {"center": v(-7.5, -33.4) * mm, "radius": 2.43 * mm});
            skCircle(sketch, "E359.0.2.2", {"center": v(0.5, 14.6) * mm, "radius": 2.43 * mm});
            skCircle(sketch, "E359.0.2.3", {"center": v(0.5, 6.6) * mm, "radius": 2.43 * mm});
            skCircle(sketch, "E359.0.2.4", {"center": v(0.5, -1.4) * mm, "radius": 2.43 * mm});
            skCircle(sketch, "E359.0.2.5", {"center": v(0.5, -9.4) * mm, "radius": 2.43 * mm});
            skCircle(sketch, "E359.0.2.6", {"center": v(0.5, -17.4) * mm, "radius": 2.43 * mm});
            skCircle(sketch, "E359.0.2.7", {"center": v(0.5, -25.4) * mm, "radius": 2.43 * mm});
            skCircle(sketch, "E359.0.2.8", {"center": v(0.5, -33.4) * mm, "radius": 2.43 * mm});
            skCircle(sketch, "E359.0.3.2", {"center": v(8.5, 14.6) * mm, "radius": 2.43 * mm});
            skCircle(sketch, "E359.0.3.3", {"center": v(8.5, 6.6) * mm, "radius": 2.43 * mm});
            skCircle(sketch, "E359.0.3.4", {"center": v(8.5, -1.4) * mm, "radius": 2.43 * mm});
            skCircle(sketch, "E359.0.3.5", {"center": v(8.5, -9.4) * mm, "radius": 2.43 * mm});
            skCircle(sketch, "E359.0.3.6", {"center": v(8.5, -17.4) * mm, "radius": 2.43 * mm});
            skCircle(sketch, "E359.0.3.7", {"center": v(8.5, -25.4) * mm, "radius": 2.43 * mm});
            skCircle(sketch, "E359.0.3.8", {"center": v(8.5, -33.4) * mm, "radius": 2.43 * mm});
            skCircle(sketch, "E359.0.4.2", {"center": v(16.5, 14.6) * mm, "radius": 2.43 * mm});
            skCircle(sketch, "E359.0.4.3", {"center": v(16.5, 6.6) * mm, "radius": 2.43 * mm});
            skCircle(sketch, "E359.0.4.4", {"center": v(16.5, -1.4) * mm, "radius": 2.43 * mm});
            skCircle(sketch, "E359.0.4.5", {"center": v(16.5, -9.4) * mm, "radius": 2.43 * mm});
            skCircle(sketch, "E359.0.4.6", {"center": v(16.5, -17.4) * mm, "radius": 2.43 * mm});
            skCircle(sketch, "E359.0.4.7", {"center": v(16.5, -25.4) * mm, "radius": 2.43 * mm});
            skCircle(sketch, "E359.0.4.8", {"center": v(16.5, -33.4) * mm, "radius": 2.43 * mm});
            skSolve(sketch);
        }
        {
            var Q0;
            Q0 = qSketchRegion(id + "F3", true);
            extrude(context, id + "F4", {"entities" : qUnion([Q0]), "operationType" : NewBodyOperationType.REMOVE, "oppositeDirection" : true, "depth" : 3 * mm, "offsetDistance" : 25 * mm});
        }
        {
            var Q0;
            Q0=makeQuery(id+"F2.opExtrude","CAP_FACE",FACE,{"disambiguationData":[OSD([sQuery(id+"F1.wireOp",EDGE,"E347"),sQuery(id+"F1.wireOp",EDGE,"E348"),sQuery(id+"F1.wireOp",EDGE,"E349.0"),sQuery(id+"F1.wireOp",EDGE,"E349.1"),sQuery(id+"F1.wireOp",EDGE,"E349.2"),sQuery(id+"F1.wireOp",EDGE,"E349.3"),sQuery(id+"F1.wireOp",EDGE,"E350.filletArc"),sQuery(id+"F1.wireOp",EDGE,"E351.filletArc"),sQuery(id+"F1.wireOp",EDGE,"E352.filletArc"),sQuery(id+"F1.wireOp",EDGE,"E353.filletArc")])],"isStart":false});
            var sketch = newSketch(context, id + "F5", { "sketchPlane" : qUnion([Q0])});
            skCircle(sketch, "E360.0", {"center": v(-10.17, -10.53) * mm, "radius": 0.5 * mm});
            skCircle(sketch, "E361.0", {"center": v(-10.17, -10.53) * mm, "radius": 2.5 * mm});
            skCircle(sketch, "E362.0", {"center": v(2.53, 27.57) * mm, "radius": 0.5 * mm});
            skCircle(sketch, "E363.0", {"center": v(2.53, 27.57) * mm, "radius": 2.5 * mm});
            skSolve(sketch);
        }
        {
            var Q0;
            Q0 = qSketchRegion(id + "F5", true);
            extrude(context, id + "F6", {"entities" : qUnion([Q0]), "operationType" : NewBodyOperationType.ADD, "depth" : 2 * mm, "offsetDistance" : 25 * mm});
        }
        {
            var Q0;
            Q0=makeQuery(id+"F2.opExtrude","CAP_FACE",FACE,{"disambiguationData":[OSD([sQuery(id+"F1.wireOp",EDGE,"E347"),sQuery(id+"F1.wireOp",EDGE,"E348"),sQuery(id+"F1.wireOp",EDGE,"E349.0"),sQuery(id+"F1.wireOp",EDGE,"E349.1"),sQuery(id+"F1.wireOp",EDGE,"E349.2"),sQuery(id+"F1.wireOp",EDGE,"E349.3"),sQuery(id+"F1.wireOp",EDGE,"E350.filletArc"),sQuery(id+"F1.wireOp",EDGE,"E351.filletArc"),sQuery(id+"F1.wireOp",EDGE,"E352.filletArc"),sQuery(id+"F1.wireOp",EDGE,"E353.filletArc")])],"isStart":false});
            var sketch = newSketch(context, id + "F7", { "sketchPlane" : qUnion([Q0])});
            skLineSegment(sketch, "E364.0", {"start": v(-17, -34.6) * mm, "end": v(18, -34.6) * mm});
            skArc(sketch, "E364.1", {"start": v(-19.5, -32.1) * mm, "mid": v(-18.77, -33.86) * mm, "end": v(-17, -34.6) * mm});
            skLineSegment(sketch, "E364.2", {"start": v(-19.5, -32.1) * mm, "end": v(-19.5, 34.9) * mm});
            skArc(sketch, "E364.3", {"start": v(-17, 37.4) * mm, "mid": v(-18.77, 36.68) * mm, "end": v(-19.5, 34.9) * mm});
            skLineSegment(sketch, "E364.4", {"start": v(-17, 37.4) * mm, "end": v(18, 37.4) * mm});
            skArc(sketch, "E364.5", {"start": v(20.5, 34.9) * mm, "mid": v(19.77, 36.68) * mm, "end": v(18, 37.4) * mm});
            skLineSegment(sketch, "E364.6", {"start": v(20.5, -32.1) * mm, "end": v(20.5, 34.9) * mm});
            skArc(sketch, "E364.7", {"start": v(18, -34.6) * mm, "mid": v(19.77, -33.86) * mm, "end": v(20.5, -32.1) * mm});
            skArc(sketch, "E365.0", {"start": v(-17.5, -32.1) * mm, "mid": v(-17.36, -32.44) * mm, "end": v(-17, -32.6) * mm});
            skLineSegment(sketch, "E365.1", {"start": v(-17, -32.6) * mm, "end": v(18, -32.6) * mm});
            skLineSegment(sketch, "E365.2", {"start": v(-17.5, -32.1) * mm, "end": v(-17.5, 34.9) * mm});
            skArc(sketch, "E365.3", {"start": v(18, -32.6) * mm, "mid": v(18.35, -32.44) * mm, "end": v(18.5, -32.1) * mm});
            skArc(sketch, "E365.4", {"start": v(-17, 35.4) * mm, "mid": v(-17.36, 35.26) * mm, "end": v(-17.5, 34.9) * mm});
            skLineSegment(sketch, "E365.5", {"start": v(-17, 35.4) * mm, "end": v(18, 35.4) * mm});
            skArc(sketch, "E365.6", {"start": v(18.5, 34.9) * mm, "mid": v(18.35, 35.26) * mm, "end": v(18, 35.4) * mm});
            skLineSegment(sketch, "E365.7", {"start": v(18.5, -32.1) * mm, "end": v(18.5, 34.9) * mm});
            skSolve(sketch);
        }
        {
            var Q0;
            Q0 = qSketchRegion(id + "F7", true);
            extrude(context, id + "F8", {"entities" : qUnion([Q0]), "operationType" : NewBodyOperationType.ADD, "depth" : 25 * mm, "offsetDistance" : 25 * mm});
        }
        {
            var Q0;
            Q0=makeQuery(id+"F8.boolean.opBoolean","MERGE",FACE,{"derivedFrom":[makeQuery(id+"F2.opExtrude","SWEPT_FACE",FACE,{"disambiguationData":[OSD([sQuery(id+"F1.wireOp",EDGE,"E349.0")])]}),makeQuery(id+"F8.opExtrude","SWEPT_FACE",FACE,{"disambiguationData":[OSD([sQuery(id+"F7.wireOp",EDGE,"E364.4")])]})]});
            var sketch = newSketch(context, id + "F9", { "sketchPlane" : qUnion([Q0])});
            skLineSegment(sketch, "E366.0", {"start": v(-5.03, 5) * mm, "end": v(-0.03, 5) * mm, "construction": true});
            skPoint(sketch, "E366.1", {"position": v(12.71, 0) * mm});
            skPoint(sketch, "E367.firstSnap0", {"position": v(-2.53, 5) * mm});
            skLineSegment(sketch, "E367.bottom", {"start": v(12.71, 5) * mm, "end": v(-0.29, 5) * mm});
            skLineSegment(sketch, "E367.top", {"start": v(10.71, 18) * mm, "end": v(1.71, 18) * mm});
            skLineSegment(sketch, "E367.left", {"start": v(12.71, 5) * mm, "end": v(12.71, 16) * mm});
            skLineSegment(sketch, "E367.right", {"start": v(-0.29, 5) * mm, "end": v(-0.29, 16) * mm});
            skPoint(sketch, "E368.visualSharp", {"position": v(-0.29, 18) * mm});
            skArc(sketch, "E368.filletArc", {"start": v(1.71, 18) * mm, "mid": v(0.3, 17.41) * mm, "end": v(-0.29, 16) * mm});
            skPoint(sketch, "E369.visualSharp", {"position": v(12.71, 18) * mm});
            skArc(sketch, "E369.filletArc", {"start": v(12.71, 16) * mm, "mid": v(12.13, 17.41) * mm, "end": v(10.71, 18) * mm});
            skSolve(sketch);
        }
        {
            var Q0;
            Q0 = qSketchRegion(id + "F9", true);
            extrude(context, id + "F10", {"entities" : qUnion([Q0]), "operationType" : NewBodyOperationType.REMOVE, "endBound" : BoundingType.UP_TO_NEXT, "oppositeDirection" : true, "depth" : 25 * mm, "offsetDistance" : 25 * mm});
        }
        {
            var Q0;
            Q0=makeQuery(id+"F8.boolean.opBoolean","MERGE",FACE,{"derivedFrom":[makeQuery(id+"F2.opExtrude","SWEPT_FACE",FACE,{"disambiguationData":[OSD([sQuery(id+"F1.wireOp",EDGE,"E349.3")])]}),makeQuery(id+"F8.opExtrude","SWEPT_FACE",FACE,{"disambiguationData":[OSD([sQuery(id+"F7.wireOp",EDGE,"E364.6")])]})]});
            var sketch = newSketch(context, id + "F11", { "sketchPlane" : qUnion([Q0])});
            skPoint(sketch, "E370.0", {"position": v(29.1, 0) * mm});
            skLineSegment(sketch, "E371.bottom", {"start": v(28.45, 28) * mm, "end": v(29.75, 28) * mm});
            skLineSegment(sketch, "E371.top", {"start": v(28.45, 23) * mm, "end": v(29.75, 23) * mm});
            skLineSegment(sketch, "E371.left", {"start": v(28.45, 28) * mm, "end": v(28.45, 23) * mm});
            skLineSegment(sketch, "E371.right", {"start": v(29.75, 28) * mm, "end": v(29.75, 23) * mm});
            skPoint(sketch, "E371.middle", {"position": v(29.1, 25.5) * mm});
            skLineSegment(sketch, "E372.1.0.0", {"start": v(27.2, 28) * mm, "end": v(27.2, 23) * mm});
            skLineSegment(sketch, "E372.1.0.1", {"start": v(25.9, 28) * mm, "end": v(25.9, 23) * mm});
            skLineSegment(sketch, "E372.1.0.2", {"start": v(25.9, 23) * mm, "end": v(27.2, 23) * mm});
            skLineSegment(sketch, "E372.1.0.3", {"start": v(25.9, 28) * mm, "end": v(27.2, 28) * mm});
            skPoint(sketch, "E372.1.0.4", {"position": v(26.56, 25.5) * mm});
            skLineSegment(sketch, "E372.2.0.0", {"start": v(24.67, 28) * mm, "end": v(24.67, 23) * mm});
            skLineSegment(sketch, "E372.2.0.1", {"start": v(23.37, 28) * mm, "end": v(23.37, 23) * mm});
            skLineSegment(sketch, "E372.2.0.2", {"start": v(23.37, 23) * mm, "end": v(24.67, 23) * mm});
            skLineSegment(sketch, "E372.2.0.3", {"start": v(23.37, 28) * mm, "end": v(24.67, 28) * mm});
            skPoint(sketch, "E372.2.0.4", {"position": v(24.02, 25.5) * mm});
            skLineSegment(sketch, "E372.3.0.0", {"start": v(22.13, 28) * mm, "end": v(22.13, 23) * mm});
            skLineSegment(sketch, "E372.3.0.1", {"start": v(20.83, 28) * mm, "end": v(20.83, 23) * mm});
            skLineSegment(sketch, "E372.3.0.2", {"start": v(20.83, 23) * mm, "end": v(22.13, 23) * mm});
            skLineSegment(sketch, "E372.3.0.3", {"start": v(20.83, 28) * mm, "end": v(22.13, 28) * mm});
            skPoint(sketch, "E372.3.0.4", {"position": v(21.48, 25.5) * mm});
            skLineSegment(sketch, "E372.4.0.0", {"start": v(19.59, 28) * mm, "end": v(19.59, 23) * mm});
            skLineSegment(sketch, "E372.4.0.1", {"start": v(18.29, 28) * mm, "end": v(18.29, 23) * mm});
            skLineSegment(sketch, "E372.4.0.2", {"start": v(18.29, 23) * mm, "end": v(19.59, 23) * mm});
            skLineSegment(sketch, "E372.4.0.3", {"start": v(18.29, 28) * mm, "end": v(19.59, 28) * mm});
            skPoint(sketch, "E372.4.0.4", {"position": v(18.94, 25.5) * mm});
            skLineSegment(sketch, "E372.5.0.0", {"start": v(17.05, 28) * mm, "end": v(17.05, 23) * mm});
            skLineSegment(sketch, "E372.5.0.1", {"start": v(15.75, 28) * mm, "end": v(15.75, 23) * mm});
            skLineSegment(sketch, "E372.5.0.2", {"start": v(15.75, 23) * mm, "end": v(17.05, 23) * mm});
            skLineSegment(sketch, "E372.5.0.3", {"start": v(15.75, 28) * mm, "end": v(17.05, 28) * mm});
            skPoint(sketch, "E372.5.0.4", {"position": v(16.4, 25.5) * mm});
            skLineSegment(sketch, "E372.6.0.0", {"start": v(14.5, 28) * mm, "end": v(14.5, 23) * mm});
            skLineSegment(sketch, "E372.6.0.1", {"start": v(13.2, 28) * mm, "end": v(13.2, 23) * mm});
            skLineSegment(sketch, "E372.6.0.2", {"start": v(13.2, 23) * mm, "end": v(14.5, 23) * mm});
            skLineSegment(sketch, "E372.6.0.3", {"start": v(13.2, 28) * mm, "end": v(14.5, 28) * mm});
            skPoint(sketch, "E372.6.0.4", {"position": v(13.86, 25.5) * mm});
            skLineSegment(sketch, "E372.7.0.0", {"start": v(11.97, 28) * mm, "end": v(11.97, 23) * mm});
            skLineSegment(sketch, "E372.7.0.1", {"start": v(10.67, 28) * mm, "end": v(10.67, 23) * mm});
            skLineSegment(sketch, "E372.7.0.2", {"start": v(10.67, 23) * mm, "end": v(11.97, 23) * mm});
            skLineSegment(sketch, "E372.7.0.3", {"start": v(10.67, 28) * mm, "end": v(11.97, 28) * mm});
            skPoint(sketch, "E372.7.0.4", {"position": v(11.32, 25.5) * mm});
            skLineSegment(sketch, "E372.8.0.0", {"start": v(9.43, 28) * mm, "end": v(9.43, 23) * mm});
            skLineSegment(sketch, "E372.8.0.1", {"start": v(8.13, 28) * mm, "end": v(8.13, 23) * mm});
            skLineSegment(sketch, "E372.8.0.2", {"start": v(8.13, 23) * mm, "end": v(9.43, 23) * mm});
            skLineSegment(sketch, "E372.8.0.3", {"start": v(8.13, 28) * mm, "end": v(9.43, 28) * mm});
            skPoint(sketch, "E372.8.0.4", {"position": v(8.78, 25.5) * mm});
            skLineSegment(sketch, "E372.9.0.0", {"start": v(6.89, 28) * mm, "end": v(6.89, 23) * mm});
            skLineSegment(sketch, "E372.9.0.1", {"start": v(5.59, 28) * mm, "end": v(5.59, 23) * mm});
            skLineSegment(sketch, "E372.9.0.2", {"start": v(5.59, 23) * mm, "end": v(6.89, 23) * mm});
            skLineSegment(sketch, "E372.9.0.3", {"start": v(5.59, 28) * mm, "end": v(6.89, 28) * mm});
            skPoint(sketch, "E372.9.0.4", {"position": v(6.24, 25.5) * mm});
            skLineSegment(sketch, "E372.10.0.0", {"start": v(4.35, 28) * mm, "end": v(4.35, 23) * mm});
            skLineSegment(sketch, "E372.10.0.1", {"start": v(3.05, 28) * mm, "end": v(3.05, 23) * mm});
            skLineSegment(sketch, "E372.10.0.2", {"start": v(3.05, 23) * mm, "end": v(4.35, 23) * mm});
            skLineSegment(sketch, "E372.10.0.3", {"start": v(3.05, 28) * mm, "end": v(4.35, 28) * mm});
            skPoint(sketch, "E372.10.0.4", {"position": v(3.7, 25.5) * mm});
            skLineSegment(sketch, "E372.11.0.0", {"start": v(1.8, 28) * mm, "end": v(1.8, 23) * mm});
            skLineSegment(sketch, "E372.11.0.1", {"start": v(0.5, 28) * mm, "end": v(0.5, 23) * mm});
            skLineSegment(sketch, "E372.11.0.2", {"start": v(0.5, 23) * mm, "end": v(1.8, 23) * mm});
            skLineSegment(sketch, "E372.11.0.3", {"start": v(0.5, 28) * mm, "end": v(1.8, 28) * mm});
            skPoint(sketch, "E372.11.0.4", {"position": v(1.16, 25.5) * mm});
            skLineSegment(sketch, "E372.12.0.0", {"start": v(-0.73, 28) * mm, "end": v(-0.73, 23) * mm});
            skLineSegment(sketch, "E372.12.0.1", {"start": v(-2.03, 28) * mm, "end": v(-2.03, 23) * mm});
            skLineSegment(sketch, "E372.12.0.2", {"start": v(-2.03, 23) * mm, "end": v(-0.73, 23) * mm});
            skLineSegment(sketch, "E372.12.0.3", {"start": v(-2.03, 28) * mm, "end": v(-0.73, 28) * mm});
            skPoint(sketch, "E372.12.0.4", {"position": v(-1.38, 25.5) * mm});
            skLineSegment(sketch, "E372.13.0.0", {"start": v(-3.27, 28) * mm, "end": v(-3.27, 23) * mm});
            skLineSegment(sketch, "E372.13.0.1", {"start": v(-4.57, 28) * mm, "end": v(-4.57, 23) * mm});
            skLineSegment(sketch, "E372.13.0.2", {"start": v(-4.57, 23) * mm, "end": v(-3.27, 23) * mm});
            skLineSegment(sketch, "E372.13.0.3", {"start": v(-4.57, 28) * mm, "end": v(-3.27, 28) * mm});
            skPoint(sketch, "E372.13.0.4", {"position": v(-3.92, 25.5) * mm});
            skLineSegment(sketch, "E372.14.0.0", {"start": v(-5.81, 28) * mm, "end": v(-5.81, 23) * mm});
            skLineSegment(sketch, "E372.14.0.1", {"start": v(-7.11, 28) * mm, "end": v(-7.11, 23) * mm});
            skLineSegment(sketch, "E372.14.0.2", {"start": v(-7.11, 23) * mm, "end": v(-5.81, 23) * mm});
            skLineSegment(sketch, "E372.14.0.3", {"start": v(-7.11, 28) * mm, "end": v(-5.81, 28) * mm});
            skPoint(sketch, "E372.14.0.4", {"position": v(-6.46, 25.5) * mm});
            skLineSegment(sketch, "E372.15.0.0", {"start": v(-8.35, 28) * mm, "end": v(-8.35, 23) * mm});
            skLineSegment(sketch, "E372.15.0.1", {"start": v(-9.65, 28) * mm, "end": v(-9.65, 23) * mm});
            skLineSegment(sketch, "E372.15.0.2", {"start": v(-9.65, 23) * mm, "end": v(-8.35, 23) * mm});
            skLineSegment(sketch, "E372.15.0.3", {"start": v(-9.65, 28) * mm, "end": v(-8.35, 28) * mm});
            skPoint(sketch, "E372.15.0.4", {"position": v(-9, 25.5) * mm});
            skLineSegment(sketch, "E372.16.0.0", {"start": v(-10.9, 28) * mm, "end": v(-10.9, 23) * mm});
            skLineSegment(sketch, "E372.16.0.1", {"start": v(-12.2, 28) * mm, "end": v(-12.2, 23) * mm});
            skLineSegment(sketch, "E372.16.0.2", {"start": v(-12.2, 23) * mm, "end": v(-10.9, 23) * mm});
            skLineSegment(sketch, "E372.16.0.3", {"start": v(-12.2, 28) * mm, "end": v(-10.9, 28) * mm});
            skPoint(sketch, "E372.16.0.4", {"position": v(-11.54, 25.5) * mm});
            skLineSegment(sketch, "E372.17.0.0", {"start": v(-13.43, 28) * mm, "end": v(-13.43, 23) * mm});
            skLineSegment(sketch, "E372.17.0.1", {"start": v(-14.73, 28) * mm, "end": v(-14.73, 23) * mm});
            skLineSegment(sketch, "E372.17.0.2", {"start": v(-14.73, 23) * mm, "end": v(-13.43, 23) * mm});
            skLineSegment(sketch, "E372.17.0.3", {"start": v(-14.73, 28) * mm, "end": v(-13.43, 28) * mm});
            skPoint(sketch, "E372.17.0.4", {"position": v(-14.08, 25.5) * mm});
            skLineSegment(sketch, "E372.direction1", {"start": v(28.45, 23) * mm, "end": v(25.9, 23) * mm, "construction": true});
            skLineSegment(sketch, "E373.0.18.0", {"start": v(-15.97, 28) * mm, "end": v(-15.97, 23) * mm});
            skLineSegment(sketch, "E373.3.18.0", {"start": v(-17.27, 28) * mm, "end": v(-17.27, 23) * mm});
            skLineSegment(sketch, "E373.6.18.0", {"start": v(-17.27, 23) * mm, "end": v(-15.97, 23) * mm});
            skLineSegment(sketch, "E373.9.18.0", {"start": v(-17.27, 28) * mm, "end": v(-15.97, 28) * mm});
            skPoint(sketch, "E373.12.18.0", {"position": v(-16.62, 25.5) * mm});
            skLineSegment(sketch, "E373.0.19.0", {"start": v(-18.51, 28) * mm, "end": v(-18.51, 23) * mm});
            skLineSegment(sketch, "E373.3.19.0", {"start": v(-19.81, 28) * mm, "end": v(-19.81, 23) * mm});
            skLineSegment(sketch, "E373.6.19.0", {"start": v(-19.81, 23) * mm, "end": v(-18.51, 23) * mm});
            skLineSegment(sketch, "E373.9.19.0", {"start": v(-19.81, 28) * mm, "end": v(-18.51, 28) * mm});
            skPoint(sketch, "E373.12.19.0", {"position": v(-19.16, 25.5) * mm});
            skSolve(sketch);
        }
        {
            var Q0;
            Q0 = qSketchRegion(id + "F11", true);
            extrude(context, id + "F12", {"entities" : qUnion([Q0]), "operationType" : NewBodyOperationType.REMOVE, "endBound" : BoundingType.UP_TO_NEXT, "oppositeDirection" : true, "depth" : 25 * mm, "offsetDistance" : 25 * mm});
        }
    });
